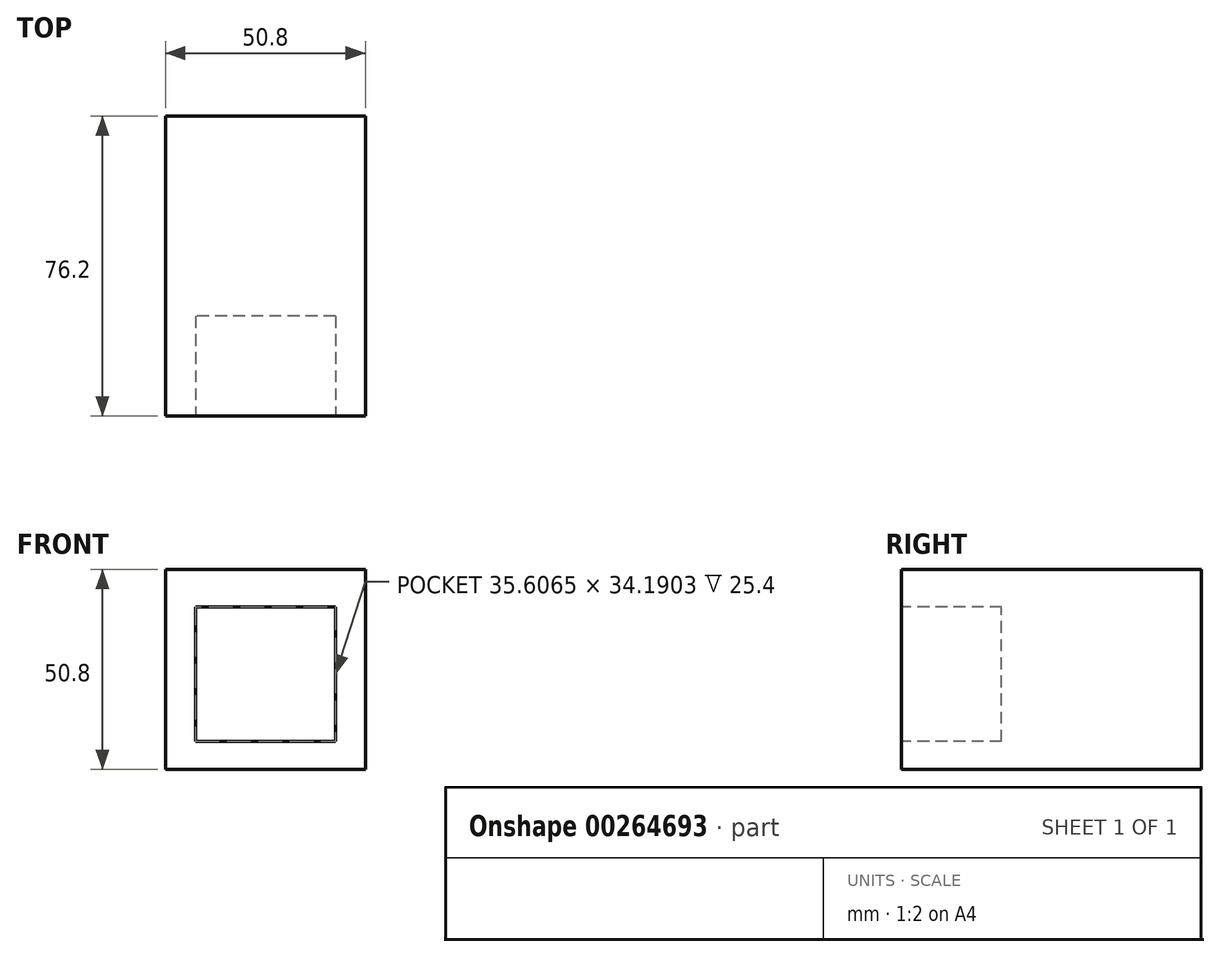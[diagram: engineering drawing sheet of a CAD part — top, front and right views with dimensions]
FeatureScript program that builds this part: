
annotation { "Feature Type Name" : "Feature", "Feature Type Description" : "" }
export const myFeature = defineFeature(function(context is Context, id is Id, definition is map)
    precondition{}
    {
        {
            var Q0;
            Q0=qCreatedBy(makeId("Front.planeOp"),FACE);
            var sketch = newSketch(context, id + "F0", { "sketchPlane" : qUnion([Q0])});
            skLineSegment(sketch, "E0.bottom", {"start": v(0, 0) * mm, "end": v(-50.8, 0) * mm});
            skLineSegment(sketch, "E0.top", {"start": v(0, 50.8) * mm, "end": v(-50.8, 50.8) * mm});
            skLineSegment(sketch, "E0.left", {"start": v(0, 0) * mm, "end": v(0, 50.8) * mm});
            skLineSegment(sketch, "E0.right", {"start": v(-50.8, 0) * mm, "end": v(-50.8, 50.8) * mm});
            skSolve(sketch);
        }
        {
            var Q0;
            Q0 = qSketchRegion(id + "F0", true);
            extrude(context, id + "F1", {"entities" : qUnion([Q0]), "depth" : 50.8 * mm});
        }
        {
            var Q0;
            Q0=makeQuery(id+"F1.opExtrude","CAP_FACE",FACE,{"disambiguationData":[OSD([sQuery(id+"F0.wireOp",EDGE,"E0.bottom"),sQuery(id+"F0.wireOp",EDGE,"E0.top"),sQuery(id+"F0.wireOp",EDGE,"E0.left"),sQuery(id+"F0.wireOp",EDGE,"E0.right")])],"isStart":false});
            extrude(context, id + "F2", {"entities" : qUnion([Q0]), "operationType" : NewBodyOperationType.ADD, "depth" : 25.4 * mm});
        }
        {
            var Q0;
            Q0=makeQuery(id+"F2.opExtrude","CAP_FACE",FACE,{"disambiguationData":[OSD([sQuery(id+"F0.wireOp",EDGE,"E0.bottom"),sQuery(id+"F0.wireOp",EDGE,"E0.top"),sQuery(id+"F0.wireOp",EDGE,"E0.left"),sQuery(id+"F0.wireOp",EDGE,"E0.right")])],"isStart":false});
            var sketch = newSketch(context, id + "F3", { "sketchPlane" : qUnion([Q0])});
            skLineSegment(sketch, "E1.bottom", {"start": v(-7.56, 7.07) * mm, "end": v(-43.17, 7.07) * mm});
            skLineSegment(sketch, "E1.top", {"start": v(-7.56, 41.26) * mm, "end": v(-43.17, 41.26) * mm});
            skLineSegment(sketch, "E1.left", {"start": v(-7.56, 7.07) * mm, "end": v(-7.56, 41.26) * mm});
            skLineSegment(sketch, "E1.right", {"start": v(-43.17, 7.07) * mm, "end": v(-43.17, 41.26) * mm});
            skSolve(sketch);
        }
        {
            var Q0;
            Q0 = qSketchRegion(id + "F3", true);
            extrude(context, id + "F4", {"entities" : qUnion([Q0]), "operationType" : NewBodyOperationType.REMOVE, "oppositeDirection" : true, "depth" : 25.4 * mm});
        }
    });
